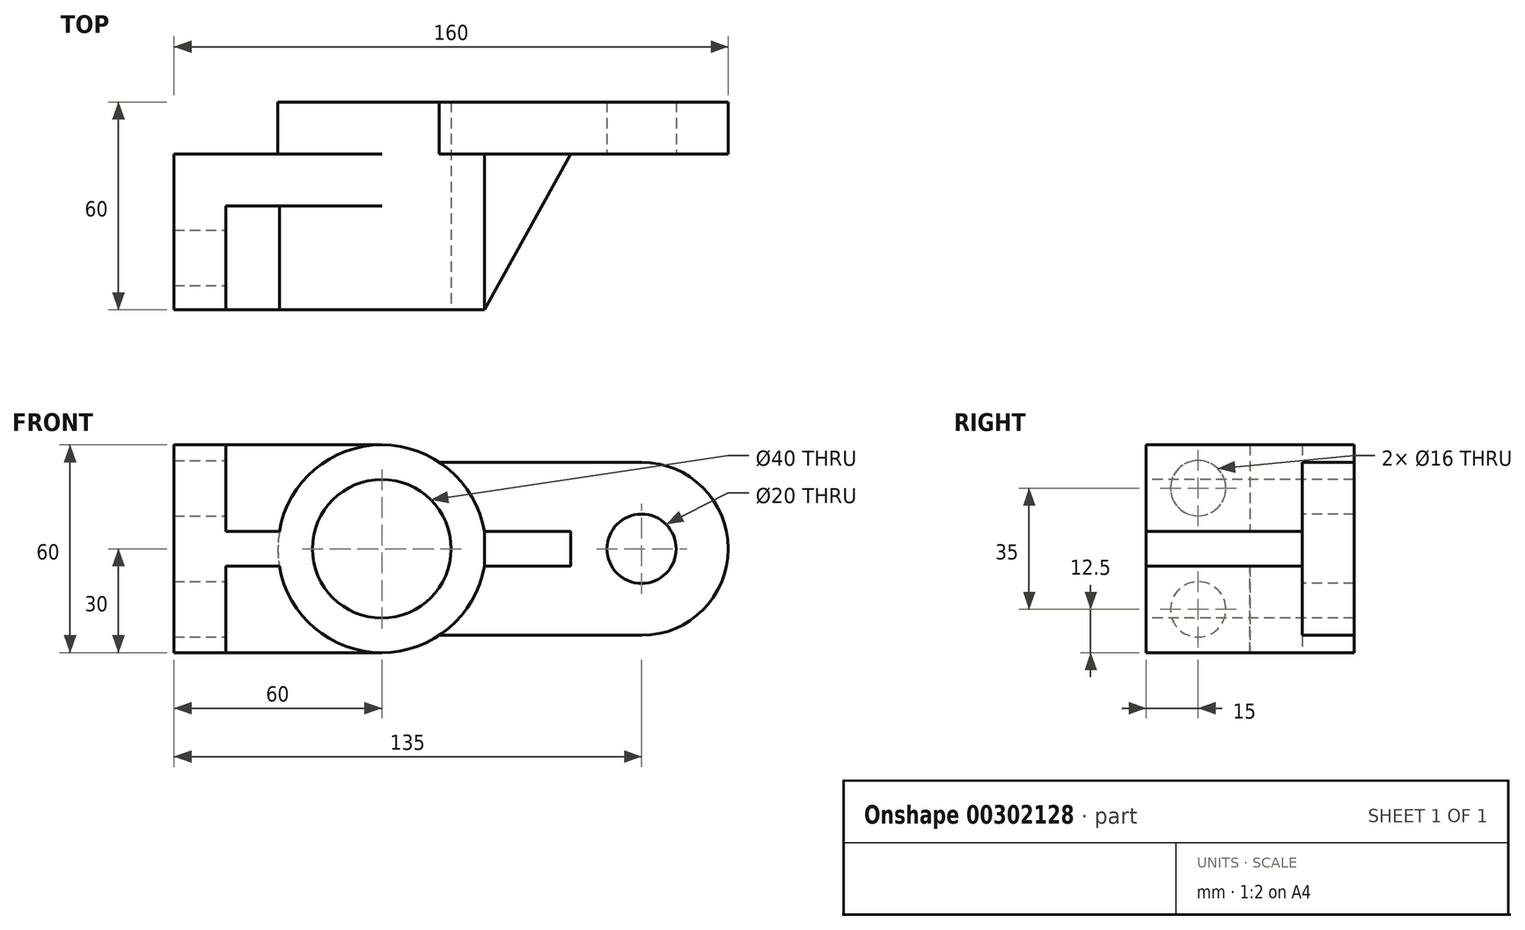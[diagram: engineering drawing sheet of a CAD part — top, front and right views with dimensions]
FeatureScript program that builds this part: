
annotation { "Feature Type Name" : "Feature", "Feature Type Description" : "" }
export const myFeature = defineFeature(function(context is Context, id is Id, definition is map)
    precondition{}
    {
        {
            var Q0;
            Q0=qCreatedBy(makeId("Front.planeOp"),FACE);
            var sketch = newSketch(context, id + "F0", { "sketchPlane" : qUnion([Q0])});
            skLineSegment(sketch, "E0", {"start": v(0, 0) * mm, "end": v(-60, 0) * mm});
            skLineSegment(sketch, "E1", {"start": v(-60, 0) * mm, "end": v(-60, 60) * mm});
            skLineSegment(sketch, "E2", {"start": v(-60, 60) * mm, "end": v(0, 60) * mm});
            skLineSegment(sketch, "E3", {"start": v(0, 60) * mm, "end": v(0, 0) * mm});
            skSolve(sketch);
        }
        {
            var Q0;
            Q0 = qSketchRegion(id + "F0", true);
            var Q1;
            Q1=makeQuery(id+"F0.imprint","IMPRINT",FACE,{"disambiguationData":[TD([[makeQuery(id+"F0.imprint","IMPRINT",EDGE,{"derivedFrom":sQuery(id+"F0.wireOp",EDGE,"E0")}),-1.0]])]});
            extrude(context, id + "F1", {"entities" : qUnion([Q0, Q1]), "depth" : 45 * mm});
        }
        {
            var Q0;
            Q0=makeQuery(id+"F1.opExtrude","CAP_FACE",FACE,{"disambiguationData":[OSD([sQuery(id+"F0.wireOp",EDGE,"E0"),sQuery(id+"F0.wireOp",EDGE,"E1"),sQuery(id+"F0.wireOp",EDGE,"E2"),sQuery(id+"F0.wireOp",EDGE,"E3")])],"isStart":false});
            var sketch = newSketch(context, id + "F2", { "sketchPlane" : qUnion([Q0])});
            skLineSegment(sketch, "E4", {"start": v(-60, 0) * mm, "end": v(-45, 0) * mm});
            skLineSegment(sketch, "E5", {"start": v(-45, 0) * mm, "end": v(-45, 25) * mm});
            skLineSegment(sketch, "E6", {"start": v(-60, 60) * mm, "end": v(-45, 60) * mm});
            skLineSegment(sketch, "E7", {"start": v(-45, 60) * mm, "end": v(-45, 35) * mm});
            skLineSegment(sketch, "E8", {"start": v(-45, 25) * mm, "end": v(0, 25) * mm});
            skLineSegment(sketch, "E9", {"start": v(-45, 35) * mm, "end": v(0, 35) * mm});
            skLineSegment(sketch, "E10", {"start": v(0, 35) * mm, "end": v(0, 25) * mm});
            skLineSegment(sketch, "E11", {"start": v(-60, 60) * mm, "end": v(-60, 0) * mm});
            skSolve(sketch);
        }
        {
            var Q0;
            {var subQ0=sQuery(id+"F2.wireOp",EDGE,"E5");Q0=makeQuery(id+"F2.imprint","IMPRINT",FACE,{"disambiguationData":[TD([[makeQuery(id+"F2.imprint","IMPRINT",EDGE,{"derivedFrom":subQ0}),-1.0]])]});}
            var Q1;
            {var subQ0=sQuery(id+"F2.wireOp",EDGE,"E7");Q1=makeQuery(id+"F2.imprint","IMPRINT",FACE,{"disambiguationData":[TD([[makeQuery(id+"F2.imprint","IMPRINT",EDGE,{"derivedFrom":subQ0}),1.0]])]});}
            extrude(context, id + "F3", {"entities" : qUnion([Q0, Q1]), "operationType" : NewBodyOperationType.REMOVE, "oppositeDirection" : true, "depth" : 30 * mm});
        }
        {
            var Q0;
            Q0=makeQuery(id+"F3.boolean.opBoolean","COPY",FACE,{"derivedFrom":makeQuery(id+"F3.opExtrude","SWEPT_FACE",FACE,{"disambiguationData":[OSD([sQuery(id+"F2.wireOp",EDGE,"E5")])]})});
            var sketch = newSketch(context, id + "F4", { "sketchPlane" : qUnion([Q0])});
            skCircle(sketch, "E12", {"center": v(-30, 12.5) * mm, "radius": 8 * mm});
            skSolve(sketch);
        }
        {
            var Q0;
            Q0 = qSketchRegion(id + "F4", true);
            extrude(context, id + "F5", {"entities" : qUnion([Q0]), "operationType" : NewBodyOperationType.REMOVE, "oppositeDirection" : true, "depth" : 15 * mm});
        }
        {
            var Q0;
            Q0=makeQuery(id+"F3.boolean.opBoolean","COPY",FACE,{"derivedFrom":makeQuery(id+"F3.opExtrude","SWEPT_FACE",FACE,{"disambiguationData":[OSD([sQuery(id+"F2.wireOp",EDGE,"E7")])]})});
            var sketch = newSketch(context, id + "F6", { "sketchPlane" : qUnion([Q0])});
            skCircle(sketch, "E13", {"center": v(-30, 47.5) * mm, "radius": 8 * mm});
            skSolve(sketch);
        }
        {
            var Q0;
            Q0 = qSketchRegion(id + "F6", true);
            extrude(context, id + "F7", {"entities" : qUnion([Q0]), "operationType" : NewBodyOperationType.REMOVE, "oppositeDirection" : true, "depth" : 25 * mm});
        }
        {
            var Q0;
            Q0=makeQuery(id+"F1.opExtrude","CAP_FACE",FACE,{"disambiguationData":[OSD([sQuery(id+"F0.wireOp",EDGE,"E0"),sQuery(id+"F0.wireOp",EDGE,"E1"),sQuery(id+"F0.wireOp",EDGE,"E2"),sQuery(id+"F0.wireOp",EDGE,"E3")])],"isStart":false});
            var sketch = newSketch(context, id + "F8", { "sketchPlane" : qUnion([Q0])});
            skCircle(sketch, "E14", {"center": v(0, 30) * mm, "radius": 30 * mm});
            skSolve(sketch);
        }
        {
            var Q0;
            Q0 = qSketchRegion(id + "F8", true);
            extrude(context, id + "F9", {"entities" : qUnion([Q0]), "operationType" : NewBodyOperationType.ADD, "oppositeDirection" : true, "depth" : 60 * mm});
        }
        {
            var Q0;
            Q0=makeQuery(id+"F9.boolean.opBoolean","MERGE",FACE,{"derivedFrom":[makeQuery(id+"F1.opExtrude","CAP_FACE",FACE,{"disambiguationData":[OSD([sQuery(id+"F0.wireOp",EDGE,"E0"),sQuery(id+"F0.wireOp",EDGE,"E1"),sQuery(id+"F0.wireOp",EDGE,"E2"),sQuery(id+"F0.wireOp",EDGE,"E3")])],"isStart":false}),makeQuery(id+"F9.opExtrude","CAP_FACE",FACE,{"disambiguationData":[OSD([sQuery(id+"F8.wireOp",EDGE,"E14")])],"isStart":true})]});
            var sketch = newSketch(context, id + "F10", { "sketchPlane" : qUnion([Q0])});
            skCircle(sketch, "E15", {"center": v(0, 30) * mm, "radius": 20 * mm});
            skSolve(sketch);
        }
        {
            var Q0;
            Q0 = qSketchRegion(id + "F10", true);
            extrude(context, id + "F11", {"entities" : qUnion([Q0]), "operationType" : NewBodyOperationType.REMOVE, "oppositeDirection" : true, "depth" : 60 * mm});
        }
        {
            var Q0;
            Q0=makeQuery(id+"F9.opExtrude","CAP_FACE",FACE,{"disambiguationData":[OSD([sQuery(id+"F8.wireOp",EDGE,"E14")])],"isStart":false});
            var sketch = newSketch(context, id + "F12", { "sketchPlane" : qUnion([Q0])});
            skLineSegment(sketch, "E16", {"start": v(-75, 30) * mm, "end": v(-75, 55) * mm});
            skLineSegment(sketch, "E17", {"start": v(-75, 30) * mm, "end": v(-75, 5) * mm});
            skLineSegment(sketch, "E18", {"start": v(-75, 5) * mm, "end": v(-16.58, 5) * mm});
            skLineSegment(sketch, "E19", {"start": v(-75, 55) * mm, "end": v(-16.58, 55) * mm});
            skArc(sketch, "E20", {"start": v(-75, 55) * mm, "mid": v(-100, 30) * mm, "end": v(-75, 5) * mm});
            skSolve(sketch);
        }
        {
            var Q0;
            Q0 = qSketchRegion(id + "F12", true);
            var Q1;
            Q1=makeQuery(id+"F12.imprint","IMPRINT",FACE,{"disambiguationData":[TD([[makeQuery(id+"F12.imprint","IMPRINT",EDGE,{"derivedFrom":sQuery(id+"F12.wireOp",EDGE,"E16")}),-1.0]])]});
            extrude(context, id + "F13", {"entities" : qUnion([Q0, Q1]), "operationType" : NewBodyOperationType.ADD, "oppositeDirection" : true, "depth" : 15 * mm});
        }
        {
            var Q0;
            Q0=makeQuery(id+"F13.opExtrude","CAP_FACE",FACE,{"disambiguationData":[OSD([sQuery(id+"F8.wireOp",EDGE,"E14"),sQuery(id+"F12.wireOp",EDGE,"E18"),sQuery(id+"F12.wireOp",EDGE,"E19"),sQuery(id+"F12.wireOp",EDGE,"E20")])],"isStart":false});
            var sketch = newSketch(context, id + "F14", { "sketchPlane" : qUnion([Q0])});
            skCircle(sketch, "E21", {"center": v(75, 30) * mm, "radius": 10 * mm});
            skSolve(sketch);
        }
        {
            var Q0;
            Q0 = qSketchRegion(id + "F14", true);
            extrude(context, id + "F15", {"entities" : qUnion([Q0]), "operationType" : NewBodyOperationType.REMOVE, "oppositeDirection" : true, "depth" : 25 * mm});
        }
        {
            var Q0;
            {var subQ0=sQuery(id+"F8.wireOp",EDGE,"E14");Q0=makeQuery(id+"F13.boolean.opBoolean","MERGE",FACE,{"derivedFrom":[makeQuery(id+"F9.opExtrude","CAP_FACE",FACE,{"disambiguationData":[OSD([subQ0])],"isStart":false}),makeQuery(id+"F13.opExtrude","CAP_FACE",FACE,{"disambiguationData":[OSD([subQ0,sQuery(id+"F12.wireOp",EDGE,"E18"),sQuery(id+"F12.wireOp",EDGE,"E19"),sQuery(id+"F12.wireOp",EDGE,"E20")])],"isStart":true})]});}
            var sketch = newSketch(context, id + "F16", { "sketchPlane" : qUnion([Q0])});
            skArc(sketch, "E22", {"start": v(-16.58, 55) * mm, "mid": v(-30, 30) * mm, "end": v(-16.58, 5) * mm});
            skLineSegment(sketch, "E23", {"start": v(-29.58, 25) * mm, "end": v(-29.58, 35) * mm});
            skLineSegment(sketch, "E24", {"start": v(-29.58, 35) * mm, "end": v(-54.58, 35) * mm});
            skLineSegment(sketch, "E25", {"start": v(-29.58, 25) * mm, "end": v(-54.58, 25) * mm});
            skLineSegment(sketch, "E26", {"start": v(-54.58, 25) * mm, "end": v(-54.58, 35) * mm});
            skSolve(sketch);
        }
        {
            var Q0;
            Q0 = qSketchRegion(id + "F16", true);
            extrude(context, id + "F17", {"entities" : qUnion([Q0]), "operationType" : NewBodyOperationType.ADD, "oppositeDirection" : true, "depth" : 60 * mm});
        }
        {
            var Q0;
            Q0=makeQuery(id+"F17.opExtrude","SWEPT_FACE",FACE,{"disambiguationData":[OSD([sQuery(id+"F16.wireOp",EDGE,"E25")])]});
            var sketch = newSketch(context, id + "F18", { "sketchPlane" : qUnion([Q0])});
            skLineSegment(sketch, "E27", {"start": v(29.58, 45) * mm, "end": v(54.58, 0) * mm});
            skLineSegment(sketch, "E28", {"start": v(54.58, 0) * mm, "end": v(54.58, 45) * mm});
            skLineSegment(sketch, "E29", {"start": v(54.58, 45) * mm, "end": v(29.58, 45) * mm});
            skSolve(sketch);
        }
        {
            var Q0;
            Q0 = qSketchRegion(id + "F18", true);
            extrude(context, id + "F19", {"entities" : qUnion([Q0]), "operationType" : NewBodyOperationType.REMOVE, "oppositeDirection" : true, "depth" : 25 * mm});
        }
    });
